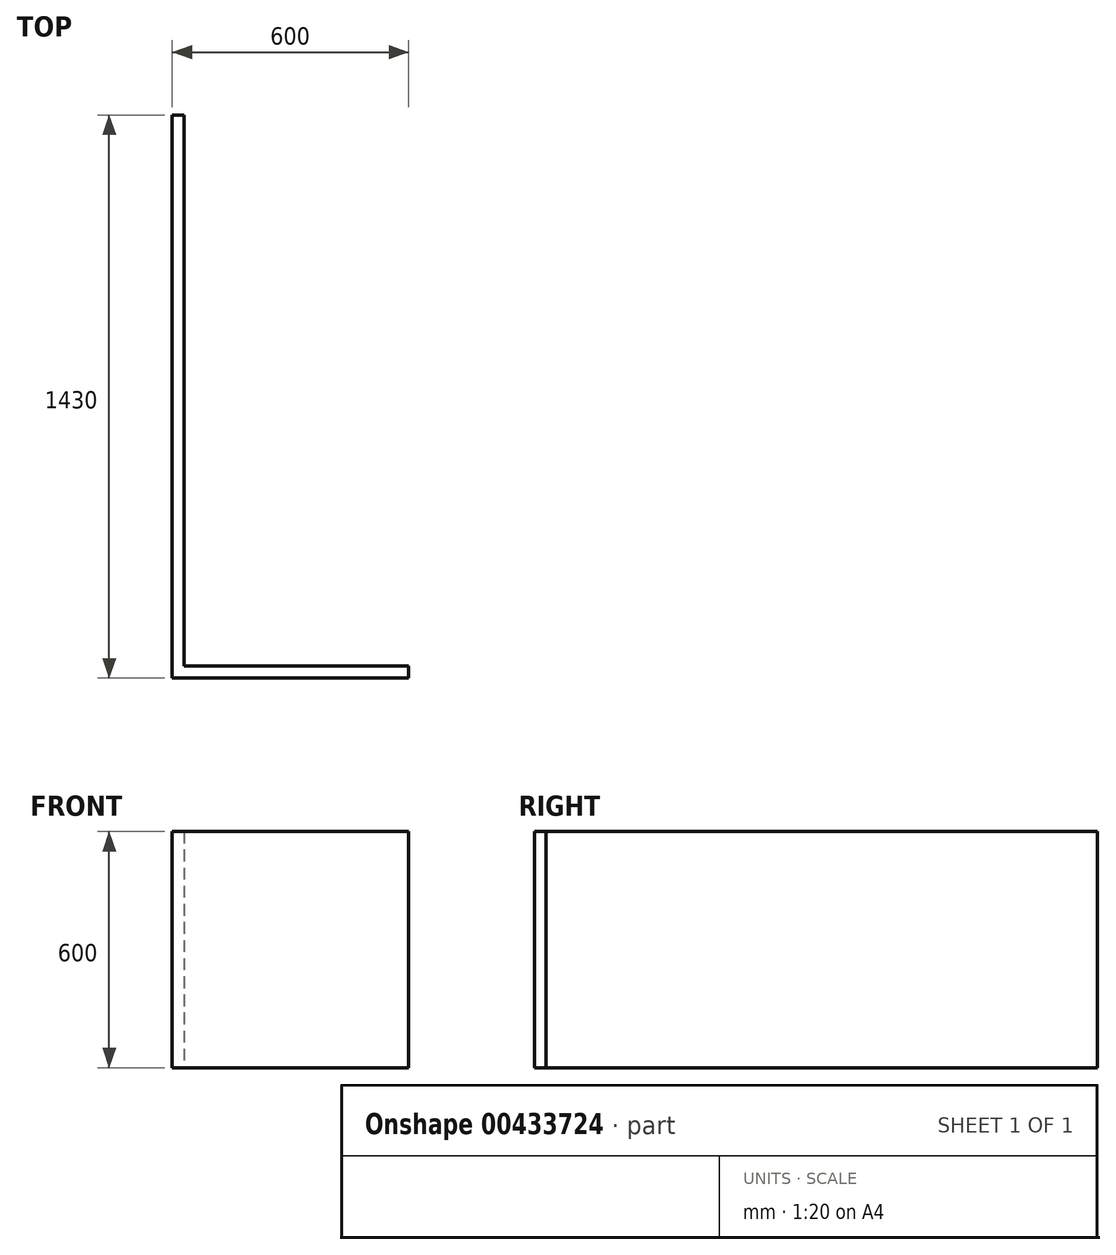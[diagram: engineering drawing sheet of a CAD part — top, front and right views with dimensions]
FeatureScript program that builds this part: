
annotation { "Feature Type Name" : "Feature", "Feature Type Description" : "" }
export const myFeature = defineFeature(function(context is Context, id is Id, definition is map)
    precondition{}
    {
        {
            var Q0;
            Q0=qCreatedBy(makeId("Front.planeOp"),FACE);
            var sketch = newSketch(context, id + "F0", { "sketchPlane" : qUnion([Q0])});
            skLineSegment(sketch, "E0.bottom", {"start": v(0, 0) * mm, "end": v(600, 0) * mm});
            skLineSegment(sketch, "E0.top", {"start": v(0, 600) * mm, "end": v(600, 600) * mm});
            skLineSegment(sketch, "E0.left", {"start": v(0, 0) * mm, "end": v(0, 600) * mm});
            skLineSegment(sketch, "E0.right", {"start": v(600, 0) * mm, "end": v(600, 600) * mm});
            skLineSegment(sketch, "E1", {"start": v(50, 600) * mm, "end": v(50, 0) * mm});
            skLineSegment(sketch, "E2", {"start": v(550, 600) * mm, "end": v(550, 0) * mm});
            skLineSegment(sketch, "E3", {"start": v(50, 550) * mm, "end": v(550, 550) * mm});
            skLineSegment(sketch, "E4", {"start": v(50, 50) * mm, "end": v(550, 50) * mm});
            skLineSegment(sketch, "E5", {"start": v(50, 325.02) * mm, "end": v(550, 325.02) * mm});
            skLineSegment(sketch, "E6", {"start": v(50, 275.02) * mm, "end": v(550, 275.02) * mm});
            skSolve(sketch);
        }
        {
            var Q0;
            {var subQ0=sQuery(id+"F0.wireOp",EDGE,"E0.left");Q0=makeQuery(id+"F0.imprint","IMPRINT",FACE,{"disambiguationData":[TD([[makeQuery(id+"F0.imprint","IMPRINT",EDGE,{"derivedFrom":subQ0}),-1.0]])]});}
            var Q1;
            {var subQ5=sQuery(id+"F0.wireOp",EDGE,"E3");Q1=makeQuery(id+"F0.imprint","IMPRINT",FACE,{"disambiguationData":[TD([[makeQuery(id+"F0.imprint","IMPRINT",EDGE,{"derivedFrom":subQ5}),1.0]])]});}
            var Q2;
            {var subQ0=sQuery(id+"F0.wireOp",EDGE,"E3");Q2=makeQuery(id+"F0.imprint","IMPRINT",FACE,{"disambiguationData":[TD([[makeQuery(id+"F0.imprint","IMPRINT",EDGE,{"derivedFrom":subQ0}),-1.0]])]});}
            var Q3;
            {var subQ0=sQuery(id+"F0.wireOp",EDGE,"E5");Q3=makeQuery(id+"F0.imprint","IMPRINT",FACE,{"disambiguationData":[TD([[makeQuery(id+"F0.imprint","IMPRINT",EDGE,{"derivedFrom":subQ0}),-1.0]])]});}
            var Q4;
            {var subQ0=sQuery(id+"F0.wireOp",EDGE,"E4");Q4=makeQuery(id+"F0.imprint","IMPRINT",FACE,{"disambiguationData":[TD([[makeQuery(id+"F0.imprint","IMPRINT",EDGE,{"derivedFrom":subQ0}),1.0]])]});}
            var Q5;
            {var subQ5=sQuery(id+"F0.wireOp",EDGE,"E4");Q5=makeQuery(id+"F0.imprint","IMPRINT",FACE,{"disambiguationData":[TD([[makeQuery(id+"F0.imprint","IMPRINT",EDGE,{"derivedFrom":subQ5}),-1.0]])]});}
            var Q6;
            {var subQ4=sQuery(id+"F0.wireOp",EDGE,"E0.right");Q6=makeQuery(id+"F0.imprint","IMPRINT",FACE,{"disambiguationData":[TD([[makeQuery(id+"F0.imprint","IMPRINT",EDGE,{"derivedFrom":subQ4}),1.0]])]});}
            extrude(context, id + "F1", {"entities" : qUnion([Q0, Q1, Q2, Q3, Q4, Q5, Q6]), "oppositeDirection" : true, "depth" : 30 * mm});
        }
        {
            var Q0;
            Q0=makeQuery(id+"F1.opExtrude","CAP_FACE",FACE,{"disambiguationData":[OSD([sQuery(id+"F0.wireOp",EDGE,"E0.bottom"),sQuery(id+"F0.wireOp",EDGE,"E0.top"),sQuery(id+"F0.wireOp",EDGE,"E0.left"),sQuery(id+"F0.wireOp",EDGE,"E0.right")])],"isStart":false});
            var sketch = newSketch(context, id + "F2", { "sketchPlane" : qUnion([Q0])});
            skLineSegment(sketch, "E7.bottom", {"start": v(0, 600) * mm, "end": v(-30, 600) * mm});
            skLineSegment(sketch, "E7.top", {"start": v(0, 0) * mm, "end": v(-30, 0) * mm});
            skLineSegment(sketch, "E7.left", {"start": v(0, 600) * mm, "end": v(0, 0) * mm});
            skLineSegment(sketch, "E7.right", {"start": v(-30, 600) * mm, "end": v(-30, 0) * mm});
            skSolve(sketch);
        }
        {
            var Q0;
            Q0=makeQuery(id+"F2.imprint","IMPRINT",FACE,{"disambiguationData":[TD([[makeQuery(id+"F2.imprint","IMPRINT",EDGE,{"derivedFrom":sQuery(id+"F2.wireOp",EDGE,"E7.bottom")}),1.0]])]});
            extrude(context, id + "F3", {"entities" : qUnion([Q0]), "operationType" : NewBodyOperationType.ADD, "depth" : 1400 * mm});
        }
    });
